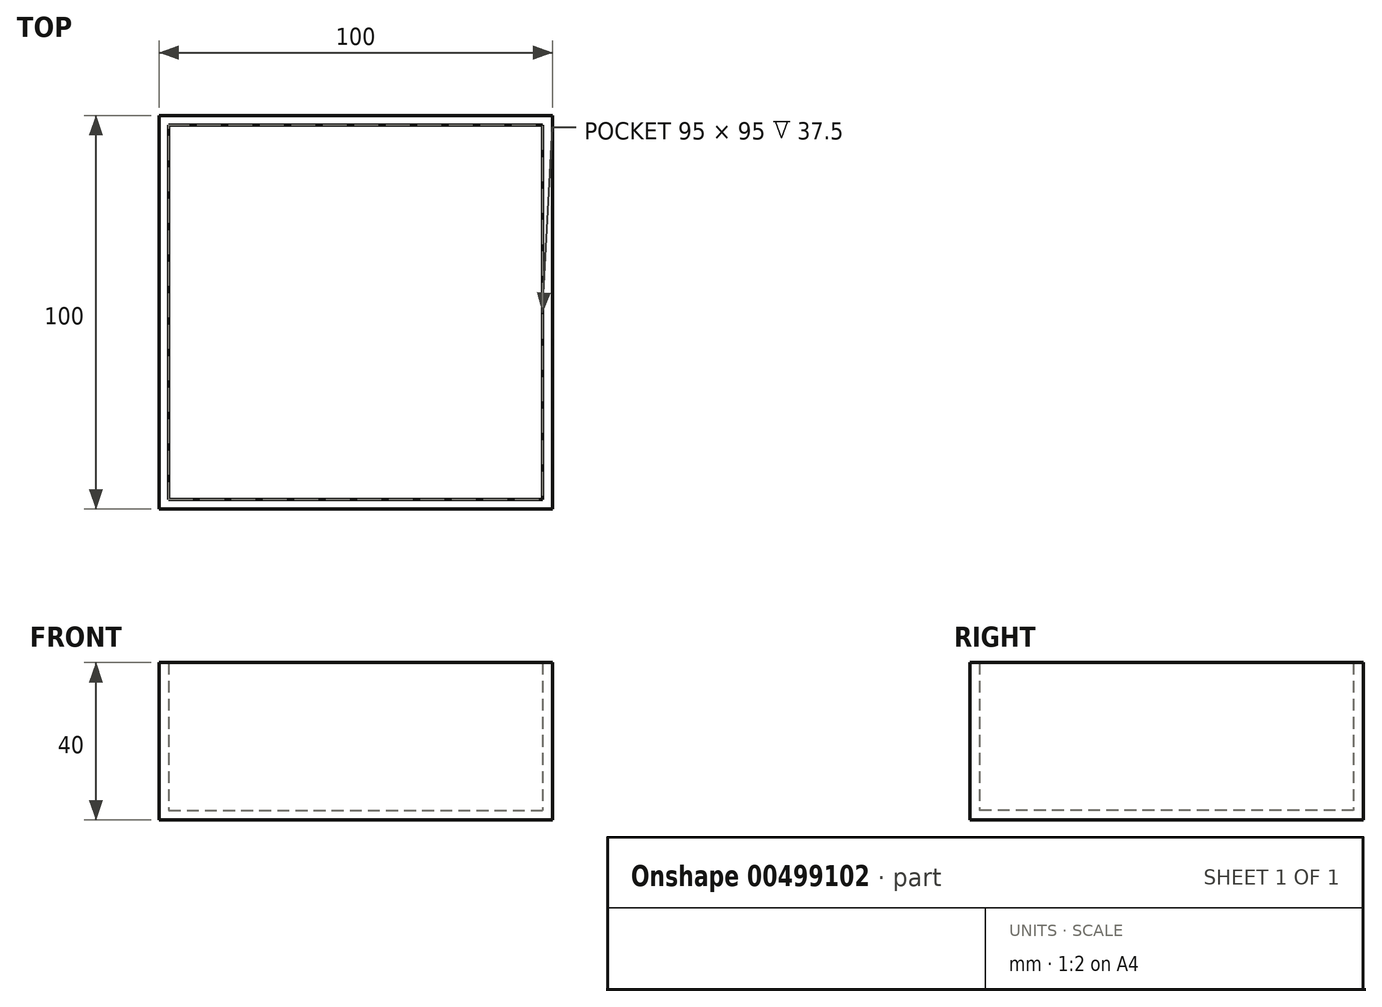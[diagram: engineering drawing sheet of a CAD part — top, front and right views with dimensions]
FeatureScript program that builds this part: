
annotation { "Feature Type Name" : "Feature", "Feature Type Description" : "" }
export const myFeature = defineFeature(function(context is Context, id is Id, definition is map)
    precondition{}
    {
        {
            var Q0;
            Q0=qCreatedBy(makeId("Top.planeOp"),FACE);
            var sketch = newSketch(context, id + "F0", { "sketchPlane" : qUnion([Q0])});
            skLineSegment(sketch, "E0.bottom", {"start": v(-50, 50) * mm, "end": v(50, 50) * mm});
            skLineSegment(sketch, "E0.top", {"start": v(-50, -50) * mm, "end": v(50, -50) * mm});
            skLineSegment(sketch, "E0.left", {"start": v(-50, 50) * mm, "end": v(-50, -50) * mm});
            skLineSegment(sketch, "E0.right", {"start": v(50, 50) * mm, "end": v(50, -50) * mm});
            skPoint(sketch, "E0.middle", {"position": v(0, 0) * mm});
            skSolve(sketch);
        }
        {
            var Q0;
            Q0=makeQuery(id+"F0.imprint","IMPRINT",FACE,{"disambiguationData":[TD([[makeQuery(id+"F0.imprint","IMPRINT",EDGE,{"derivedFrom":sQuery(id+"F0.wireOp",EDGE,"E0.bottom")}),-1.0]])]});
            extrude(context, id + "F1", {"entities" : qUnion([Q0]), "depth" : 25 * mm});
        }
        {
            var Q0;
            Q0=makeQuery(id+"F1.opExtrude","CAP_FACE",FACE,{"disambiguationData":[OSD([sQuery(id+"F0.wireOp",EDGE,"E0.bottom"),sQuery(id+"F0.wireOp",EDGE,"E0.top"),sQuery(id+"F0.wireOp",EDGE,"E0.left"),sQuery(id+"F0.wireOp",EDGE,"E0.right")])],"isStart":false});
            shell(context, id + "F2", {"entities" : qUnion([Q0]), "thickness" : 2.5 * mm});
        }
        {
            var Q0;
            Q0 = qSketchRegion(id + "F0", true);
            extrude(context, id + "F3", {"entities" : qUnion([Q0]), "operationType" : NewBodyOperationType.ADD, "depth" : 40 * mm});
        }
        {
            var Q0;
            Q0=makeQuery(id+"F3.opExtrude","CAP_FACE",FACE,{"disambiguationData":[OSD([sQuery(id+"F0.wireOp",EDGE,"E0.bottom"),sQuery(id+"F0.wireOp",EDGE,"E0.top"),sQuery(id+"F0.wireOp",EDGE,"E0.left"),sQuery(id+"F0.wireOp",EDGE,"E0.right")])],"isStart":false});
            shell(context, id + "F4", {"entities" : qUnion([Q0]), "thickness" : 2.5 * mm});
        }
    });
